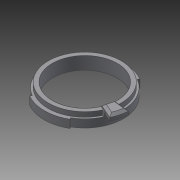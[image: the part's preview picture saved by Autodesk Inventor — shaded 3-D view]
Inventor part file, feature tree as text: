
AUTODESK INVENTOR PART (.ipt)
format: ipt  version: 2018 (Build 220112000, 112)  size: 165,376 bytes
history: native  units: mm
features: extrude x4, sketch x4, chamfer x2, other x1, mirror x1
ambient origin geometry x8: Origin, YZ Plane, XZ Plane, XY Plane, X Axis, Y Axis, Z Axis, Center Point
bodies: Body1 (feature_tree)
feature tree (12):
  other  "ソリッド1"
  extrude  "押し出し1"  Depth=5.0mm
  extrude  "押し出し2"  Depth=40.5mm
  mirror  "ミラー1"
  extrude  "押し出し7"  Depth=8.0mm TaperAngle=0.0deg
  chamfer  "面取り4"  Distance=1.2mm
  extrude  "押し出し8"  Depth=24.43461mm
  chamfer  "面取り5"  Distance=5.0mm
  sketch  "スケッチ1"
  sketch  "スケッチ2"
  sketch  "スケッチ4"
  sketch  "スケッチ7"
